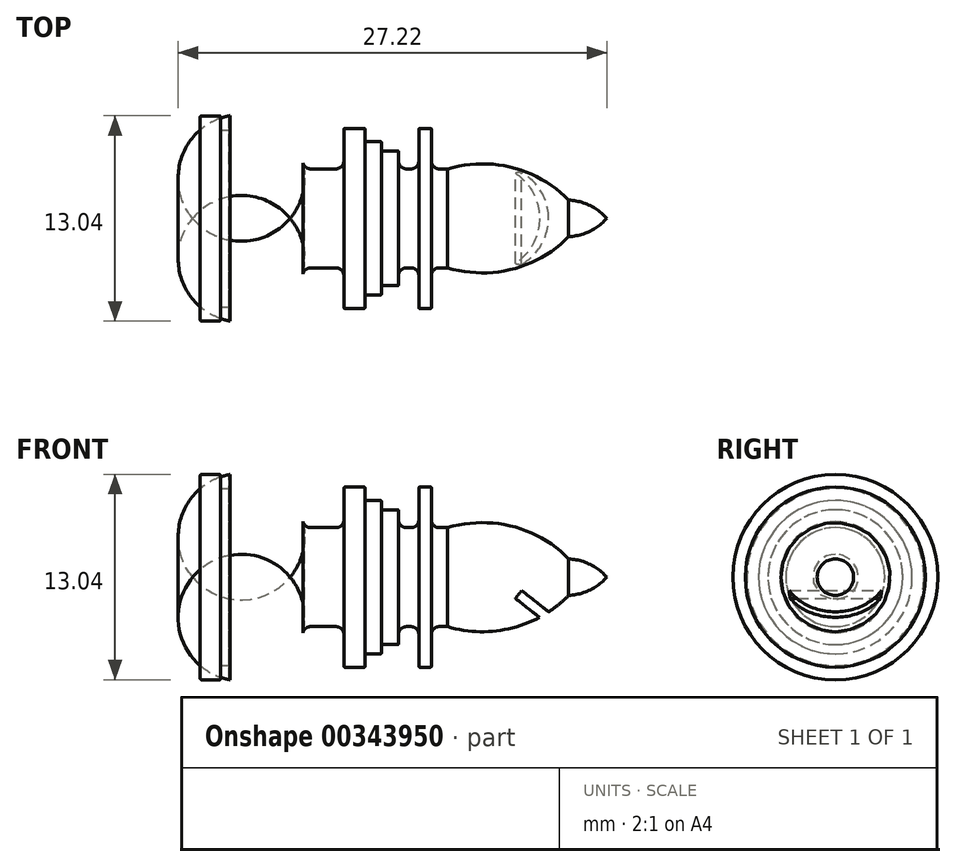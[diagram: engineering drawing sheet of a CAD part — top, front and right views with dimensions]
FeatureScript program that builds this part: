
annotation { "Feature Type Name" : "Feature", "Feature Type Description" : "" }
export const myFeature = defineFeature(function(context is Context, id is Id, definition is map)
    precondition{}
    {
        {
            var Q0;
            Q0=qCreatedBy(makeId("Front.planeOp"),FACE);
            var sketch = newSketch(context, id + "F0", { "sketchPlane" : qUnion([Q0])});
            skLineSegment(sketch, "E0", {"start": v(0, 0) * mm, "end": v(-25.82, 0) * mm});
            skLineSegment(sketch, "E1", {"start": v(-25.82, 0) * mm, "end": v(-25.82, 6.51) * mm});
            skLineSegment(sketch, "E2", {"start": v(-25.82, 6.51) * mm, "end": v(-24.53, 6.51) * mm});
            skLineSegment(sketch, "E3", {"start": v(-24.53, 6.51) * mm, "end": v(-24.53, 5.62) * mm});
            skLineSegment(sketch, "E4", {"start": v(-24.53, 5.62) * mm, "end": v(-23.98, 5.62) * mm});
            skLineSegment(sketch, "E5", {"start": v(-23.98, 5.62) * mm, "end": v(-23.98, 6.51) * mm});
            skArc(sketch, "E6", {"start": v(-19.22, 3.14) * mm, "mid": v(-20.88, 5.85) * mm, "end": v(-23.98, 6.51) * mm});
            skLineSegment(sketch, "E7", {"start": v(-19.22, 3.14) * mm, "end": v(-16.7, 3.14) * mm});
            skLineSegment(sketch, "E8", {"start": v(-16.7, 3.14) * mm, "end": v(-16.7, 5.72) * mm});
            skLineSegment(sketch, "E9", {"start": v(-16.7, 5.72) * mm, "end": v(-15.36, 5.72) * mm});
            skLineSegment(sketch, "E10", {"start": v(-15.36, 5.72) * mm, "end": v(-15.36, 4.88) * mm});
            skLineSegment(sketch, "E11", {"start": v(-15.36, 4.88) * mm, "end": v(-14.32, 4.88) * mm});
            skLineSegment(sketch, "E12", {"start": v(-14.32, 4.88) * mm, "end": v(-14.32, 4.28) * mm});
            skLineSegment(sketch, "E13", {"start": v(-14.32, 4.28) * mm, "end": v(-13.22, 4.28) * mm});
            skLineSegment(sketch, "E14", {"start": v(-13.22, 4.28) * mm, "end": v(-13.22, 3.14) * mm});
            skLineSegment(sketch, "E15", {"start": v(-13.22, 3.14) * mm, "end": v(-11.94, 3.14) * mm});
            skLineSegment(sketch, "E16", {"start": v(-11.94, 3.14) * mm, "end": v(-11.94, 5.72) * mm});
            skLineSegment(sketch, "E17", {"start": v(-11.94, 5.72) * mm, "end": v(-11.14, 5.72) * mm});
            skLineSegment(sketch, "E18", {"start": v(-11.14, 5.72) * mm, "end": v(-11.14, 3.14) * mm});
            skLineSegment(sketch, "E19", {"start": v(-11.14, 3.14) * mm, "end": v(-10.1, 3.14) * mm});
            skArc(sketch, "E20", {"start": v(-2.42, 1.16) * mm, "mid": v(-5.98, 3.22) * mm, "end": v(-10.1, 3.14) * mm});
            skArc(sketch, "E21", {"start": v(0, 0) * mm, "mid": v(-1.09, 0.83) * mm, "end": v(-2.42, 1.16) * mm});
            skSolve(sketch);
        }
        {
            var Q0;
            Q0=makeQuery(id+"F0.imprint","IMPRINT",FACE,{"disambiguationData":[TD([[makeQuery(id+"F0.imprint","IMPRINT",EDGE,{"derivedFrom":sQuery(id+"F0.wireOp",EDGE,"E0")}),-1.0]])]});
            var Q1;
            Q1=sQuery(id+"F0.wireOp",EDGE,"E0");
            revolve(context, id + "F1", {"entities" : qUnion([Q0]), "axis" : qUnion([Q1]), "revolveType" : RevolveType.FULL});
        }
        {
            var Q0;
            Q0=qCreatedBy(makeId("Front.planeOp"),FACE);
            var sketch = newSketch(context, id + "F2", { "sketchPlane" : qUnion([Q0])});
            skLineSegment(sketch, "E22", {"start": v(-2.93, -2.8) * mm, "end": v(-5.4, -0.85) * mm});
            skLineSegment(sketch, "E23", {"start": v(-5.4, -0.85) * mm, "end": v(-5.8, -1.35) * mm});
            skLineSegment(sketch, "E24", {"start": v(-5.8, -1.35) * mm, "end": v(-3.3, -3.32) * mm});
            skLineSegment(sketch, "E25", {"start": v(-3.3, -3.32) * mm, "end": v(-2.93, -2.8) * mm});
            skSolve(sketch);
        }
        {
            var Q0;
            Q0=makeQuery(id+"F2.imprint","IMPRINT",FACE,{"disambiguationData":[TD([[makeQuery(id+"F2.imprint","IMPRINT",EDGE,{"derivedFrom":sQuery(id+"F2.wireOp",EDGE,"E22")}),1.0]])]});
            extrude(context, id + "F3", {"entities" : qUnion([Q0]), "operationType" : NewBodyOperationType.REMOVE, "endBound" : BoundingType.SYMMETRIC, "depth" : 25.4 * mm});
        }
        {
            var Q0;
            Q0=makeQuery(id+"F1.opRevolve","SWEPT_EDGE",EDGE,{"disambiguationData":[OSD([sQuery(id+"F0.wireOp",EDGE,"E18"),sQuery(id+"F0.wireOp",EDGE,"E19")])]});
            var Q1;
            Q1=makeQuery(id+"F1.opRevolve","SWEPT_EDGE",EDGE,{"disambiguationData":[OSD([sQuery(id+"F0.wireOp",EDGE,"E15"),sQuery(id+"F0.wireOp",EDGE,"E16")])]});
            var Q2;
            Q2=makeQuery(id+"F1.opRevolve","SWEPT_EDGE",EDGE,{"disambiguationData":[OSD([sQuery(id+"F0.wireOp",EDGE,"E14"),sQuery(id+"F0.wireOp",EDGE,"E15")])]});
            var Q3;
            Q3=makeQuery(id+"F1.opRevolve","SWEPT_EDGE",EDGE,{"disambiguationData":[OSD([sQuery(id+"F0.wireOp",EDGE,"E7"),sQuery(id+"F0.wireOp",EDGE,"E8")])]});
            var Q4;
            Q4=makeQuery(id+"F1.opRevolve","SWEPT_EDGE",EDGE,{"disambiguationData":[OSD([sQuery(id+"F0.wireOp",EDGE,"E6"),sQuery(id+"F0.wireOp",EDGE,"E7")])]});
            fillet(context, id + "F4", {"entities" : qUnion([Q0, Q1, Q2, Q3, Q4]), "radius" : 0.5 * mm, "tangentPropagation" : true, "allowEdgeOverflow" : false});
        }
        {
            var Q0;
            Q0=makeQuery(id+"F1.opRevolve","SWEPT_EDGE",EDGE,{"disambiguationData":[OSD([sQuery(id+"F0.wireOp",EDGE,"E17"),sQuery(id+"F0.wireOp",EDGE,"E18")])]});
            var Q1;
            Q1=makeQuery(id+"F1.opRevolve","SWEPT_EDGE",EDGE,{"disambiguationData":[OSD([sQuery(id+"F0.wireOp",EDGE,"E16"),sQuery(id+"F0.wireOp",EDGE,"E17")])]});
            var Q2;
            Q2=makeQuery(id+"F1.opRevolve","SWEPT_EDGE",EDGE,{"disambiguationData":[OSD([sQuery(id+"F0.wireOp",EDGE,"E13"),sQuery(id+"F0.wireOp",EDGE,"E14")])]});
            var Q3;
            Q3=makeQuery(id+"F1.opRevolve","SWEPT_EDGE",EDGE,{"disambiguationData":[OSD([sQuery(id+"F0.wireOp",EDGE,"E11"),sQuery(id+"F0.wireOp",EDGE,"E12")])]});
            var Q4;
            Q4=makeQuery(id+"F1.opRevolve","SWEPT_EDGE",EDGE,{"disambiguationData":[OSD([sQuery(id+"F0.wireOp",EDGE,"E9"),sQuery(id+"F0.wireOp",EDGE,"E10")])]});
            var Q5;
            Q5=makeQuery(id+"F1.opRevolve","SWEPT_EDGE",EDGE,{"disambiguationData":[OSD([sQuery(id+"F0.wireOp",EDGE,"E8"),sQuery(id+"F0.wireOp",EDGE,"E9")])]});
            var Q6;
            Q6=makeQuery(id+"F1.opRevolve","SWEPT_EDGE",EDGE,{"disambiguationData":[OSD([sQuery(id+"F0.wireOp",EDGE,"E1"),sQuery(id+"F0.wireOp",EDGE,"E2")])]});
            var Q7;
            Q7=makeQuery(id+"F1.opRevolve","SWEPT_EDGE",EDGE,{"disambiguationData":[OSD([sQuery(id+"F0.wireOp",EDGE,"E2"),sQuery(id+"F0.wireOp",EDGE,"E3")])]});
            var Q8;
            Q8=makeQuery(id+"F1.opRevolve","SWEPT_EDGE",EDGE,{"disambiguationData":[OSD([sQuery(id+"F0.wireOp",EDGE,"E5"),sQuery(id+"F0.wireOp",EDGE,"E6")])]});
            fillet(context, id + "F5", {"entities" : qUnion([Q0, Q1, Q2, Q3, Q4, Q5, Q6, Q7, Q8]), "radius" : 0.05 * mm, "tangentPropagation" : true, "allowEdgeOverflow" : false});
        }
    });
